# Revit family: Bitpop 1.0A
name_source: partatom
category: Lighting Fixtures
revit_build: Autodesk Revit 2017 (Build: 20160225_1515(x64)
units: mm (PartAtom-declared; Revit-internal decimal feet)

## family parameters
Cut with Voids When Loaded = Yes
Host = Face
Light Source = Yes
Part Type = Normal
Room Calculation Point = Yes
Round Connector Dimension = Use Diameter
Shared = No

## types (8) — shared parameters
Apparent Load Phase 1 = 8 W
Body = L&L_Black anodized aluminium
CRI = 90 (also available: CRI 80 - ref. URL Technical sheet)
Code = BP1000 B 0 White; BP1000 N 0 Black; BP1010 B White; BP1010 N Black
Color Filter = 16777215
Control system = on/off; 1-10V + PUSH; DALI + PUSH
Cutout dimensions = 43x43 mm
Default Elevation = 1219 mm
Delivered lumen output = 335 lm (3000K, 30°)
Description = Indoor recessed
Dimming Lamp Color Temperature Shift = <None>
Emit from Line Length = 610 mm
Energy efficiency class = A A+ A++
Features = UGR < 10 for 17° and 30° optics
Height mm = 71 mm  [stored 0.23294 ft]
Height void = 43 mm  [stored 0.141076 ft]
IP = 40; 44 installed
LED Colour = 3000K (also available: 2700K and 4000K - ref. URL Technical sheet)
Length mm = 49 mm  [stored 0.160761 ft]
Lens = L&L_Lens
Lumen output at source = 480 lm (3000K)
Manufacturer = L&L Luce&Light
Material = body in black anodized aluminium trim in steel
Mounting = recessed (ceiling: flush or deep set)
No. and type of led = 1 high-intensity power LED
Notes = ceiling-mounted version Bitpop C
Power = 8W (also available: 6.5W - ref. URL Technical sheet)
Power cables = includes 0.30 m cable
Power supply = 230Vac (also available: 24Vdc - ref. URL Technical sheet)
Power supply unit = 230Vac: included and wired (24Vdc: not included)
Tilt Angle = 90.00°
Trim = L&L_Steel
URL = https://www.lucelight.it
URL Accessories and power supply units = https://www.lucelight.it
URL Catalogue = https://www.lucelight.it
URL DXF = https://www.lucelight.it
URL Description = https://www.lucelight.it
URL General code = https://www.lucelight.it
URL IES Photometric file = https://www.lucelight.it
URL Image = https://www.lucelight.it
URL Technical sheet = https://www.lucelight.it
Voltage = 230 V
Weight kg = 0.15
Width mm = 49 mm  [stored 0.160761 ft]
Wiring = -

## per-type parameters (varying)
| type | Geometry | Length void | Model | Optics | Photometric Web File | Width void |
| Bitpop 1.0_ F 30° (3000K 8W 230Vac) | Bitpop 1.0_mod : Bitpop 1.0 | 43 mm  [stored 0.141076 ft] | Bitpop 1.0 | 30° | BITPOP 1.0 F 30° [3000K 8W 230Vac].IES | 43 mm  [stored 0.141076 ft] |
| Bitpop 1.0_ L 42° (3000K 8W 230Vac) | Bitpop 1.0_mod : Bitpop 1.0 | 43 mm  [stored 0.141076 ft] | Bitpop 1.0 | 42° | BITPOP 1.0 L 42° [3000K 8W 230Vac].IES | 43 mm  [stored 0.141076 ft] |
| Bitpop 1.0_ S 17° (3000K 8W 230Vac) | Bitpop 1.0_mod : Bitpop 1.0 | 43 mm  [stored 0.141076 ft] | Bitpop 1.0 | 17° | BITPOP 1.0 S 17° [3000K 8W 230Vac].IES | 43 mm  [stored 0.141076 ft] |
| Bitpop 1.0_ W 17°x45° (3000K 8W 230Vac) | Bitpop 1.0_mod : Bitpop 1.0 | 43 mm  [stored 0.141076 ft] | Bitpop 1.0 | 17°x45° | BITPOP 1.0 W 17°x45° [3000K 8W 230Vac].IES | 43 mm  [stored 0.141076 ft] |
| Bitpop 1.0_Recessed_ F 30° (3000K 8W 230Vac) | Bitpop1.0_Recessed_mod : Bitpop 1.0_Recessed_mod | 52 mm | Bitpop 1.0_Recessed | 30° | BITPOP 1.0 F 30° [3000K 8W 230Vac].IES | 52 mm |
| Bitpop 1.0_Recessed_ L 42° (3000K 8W 230Vac) | Bitpop1.0_Recessed_mod : Bitpop 1.0_Recessed_mod | 52 mm | Bitpop 1.0_Recessed | 42° | BITPOP 1.0 L 42° [3000K 8W 230Vac].IES | 52 mm |
| Bitpop 1.0_Recessed_ S 17° (3000K 8W 230Vac) | Bitpop1.0_Recessed_mod : Bitpop 1.0_Recessed_mod | 52 mm | Bitpop 1.0_Recessed | 17° | BITPOP 1.0 S 17° [3000K 8W 230Vac].IES | 52 mm |
| Bitpop 1.0_Recessed_ W 17°x45° (3000K 8W 230Vac) | Bitpop1.0_Recessed_mod : Bitpop 1.0_Recessed_mod | 52 mm | Bitpop 1.0_Recessed | 17°x45° | BITPOP 1.0 W 17°x45° [3000K 8W 230Vac].IES | 52 mm |

note: [stored X ft] marks values corroborated as IEEE doubles in the binary element streams (Revit-internal decimal feet)

## geometry (parser evidence)
native form markers: Blend x2, Sweep x7
no freeform markers — native parametric forms only
